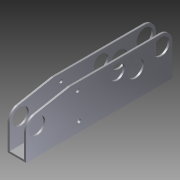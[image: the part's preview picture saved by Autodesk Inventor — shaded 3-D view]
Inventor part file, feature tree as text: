
AUTODESK INVENTOR PART (.ipt)
format: ipt  version: 2012 (Build 160160000, 160)  size: 151,552 bytes
history: native  units: in
note: dims shown in document units (in); Inventor stores cm internally (conversion verified against a paired STEP export)
features: extrude x2, sketch x2
ambient origin geometry x8: Origin, YZ Plane, XZ Plane, XY Plane, X Axis, Y Axis, Z Axis, Center Point
bodies: Solid1 (feature_tree)
feature tree (4):
  extrude  "Extrusion1"  Depth=1.25in
  extrude  "Extrusion2"  Depth=10.0in TaperAngle=0.0deg
  sketch  "Sketch1"  dims[d0=3.0in d1=1.25in]
  sketch  "Sketch2"  dims[d2=0.125in d4=10.0in d5=0.0in d8=3.0in d9=0.5in d13=0.25in d15=1.0in d16=0.0in d17=0.75in d18=1.125in d20=0.125in d21=0.125in d22=1.0in d23=0.5in d24=0.5in d25=0.5in d26=0.25in d27=0.5in d28=3.0in d29=1.0in d30=1.125in d31=1.8125in d32=0.75in d33=3.0in d34=1.125in d35=2.5in]
